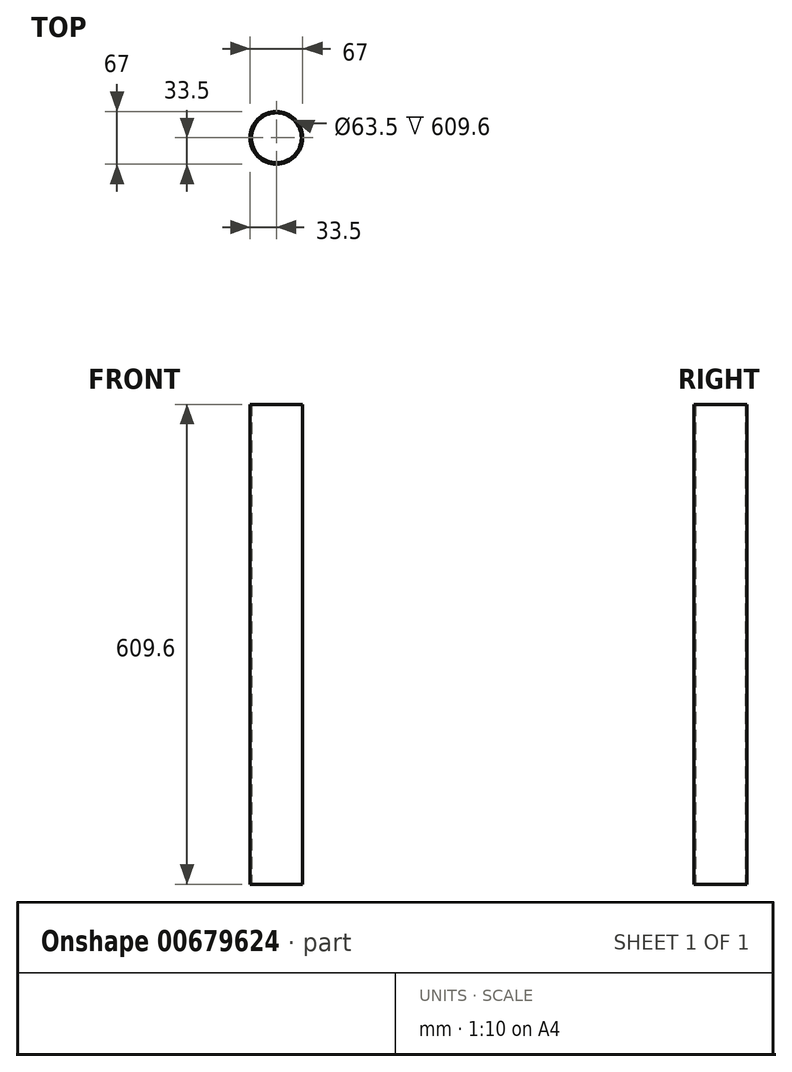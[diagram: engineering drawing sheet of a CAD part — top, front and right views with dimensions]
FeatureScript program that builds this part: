
annotation { "Feature Type Name" : "Feature", "Feature Type Description" : "" }
export const myFeature = defineFeature(function(context is Context, id is Id, definition is map)
    precondition{}
    {
        {
            var Q0;
            Q0=qCreatedBy(makeId("Top.planeOp"),FACE);
            var sketch = newSketch(context, id + "F0", { "sketchPlane" : qUnion([Q0])});
            skCircle(sketch, "E0", {"center": v(0, 0) * mm, "radius": 33.5 * mm});
            skCircle(sketch, "E1", {"center": v(0, 0) * mm, "radius": 31.75 * mm});
            skSolve(sketch);
        }
        {
            var Q0;
            Q0=makeQuery(id+"F0.imprint","IMPRINT",FACE,{"disambiguationData":[TD([[makeQuery(id+"F0.imprint","IMPRINT",EDGE,{"derivedFrom":sQuery(id+"F0.wireOp",EDGE,"E0")}),1.0]])]});
            extrude(context, id + "F1", {"entities" : qUnion([Q0]), "depth" : 609.6 * mm, "offsetDistance" : 25.4 * mm});
        }
    });
